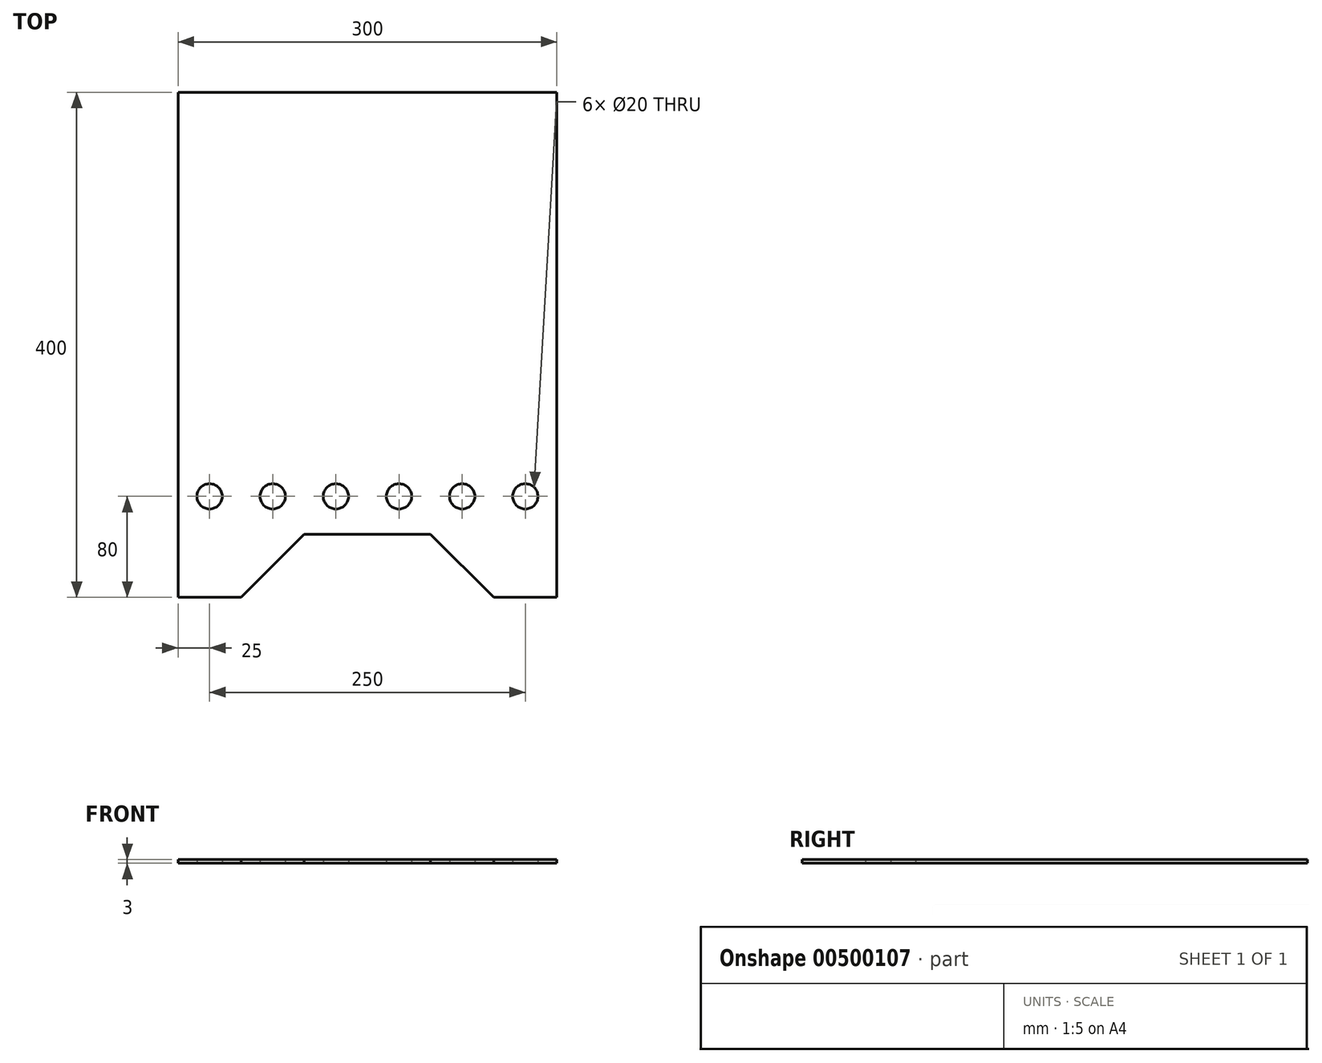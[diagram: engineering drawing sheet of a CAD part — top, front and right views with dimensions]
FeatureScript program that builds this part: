
annotation { "Feature Type Name" : "Feature", "Feature Type Description" : "" }
export const myFeature = defineFeature(function(context is Context, id is Id, definition is map)
    precondition{}
    {
        {
            var Q0;
            Q0=qCreatedBy(makeId("Top.planeOp"),FACE);
            var sketch = newSketch(context, id + "F0", { "sketchPlane" : qUnion([Q0])});
            skLineSegment(sketch, "E0.bottom", {"start": v(-150, -200) * mm, "end": v(-100, -200) * mm});
            skLineSegment(sketch, "E0.top", {"start": v(-150, 200) * mm, "end": v(150, 200) * mm});
            skLineSegment(sketch, "E0.left", {"start": v(-150, -200) * mm, "end": v(-150, 200) * mm});
            skLineSegment(sketch, "E0.right", {"start": v(150, -200) * mm, "end": v(150, 200) * mm});
            skPoint(sketch, "E0.middle", {"position": v(0, 0) * mm});
            skLineSegment(sketch, "E1", {"start": v(-100, -200) * mm, "end": v(-50, -150) * mm});
            skLineSegment(sketch, "E2", {"start": v(-50, -150) * mm, "end": v(50, -150) * mm});
            skLineSegment(sketch, "E3", {"start": v(50, -150) * mm, "end": v(100, -200) * mm});
            skLineSegment(sketch, "E4.trimOffspring", {"start": v(100, -200) * mm, "end": v(150, -200) * mm});
            skCircle(sketch, "E5", {"center": v(-125, -120) * mm, "radius": 10 * mm});
            skCircle(sketch, "E6", {"center": v(-25, -120) * mm, "radius": 10 * mm});
            skCircle(sketch, "E7", {"center": v(25, -120) * mm, "radius": 10 * mm});
            skCircle(sketch, "E8", {"center": v(75, -120) * mm, "radius": 10 * mm});
            skCircle(sketch, "E9", {"center": v(125, -120) * mm, "radius": 10 * mm});
            skCircle(sketch, "E10", {"center": v(-75, -120) * mm, "radius": 10 * mm});
            skSolve(sketch);
        }
        {
            var Q0;
            Q0 = qSketchRegion(id + "F0", true);
            extrude(context, id + "F1", {"entities" : qUnion([Q0]), "depth" : 3 * mm});
        }
    });
